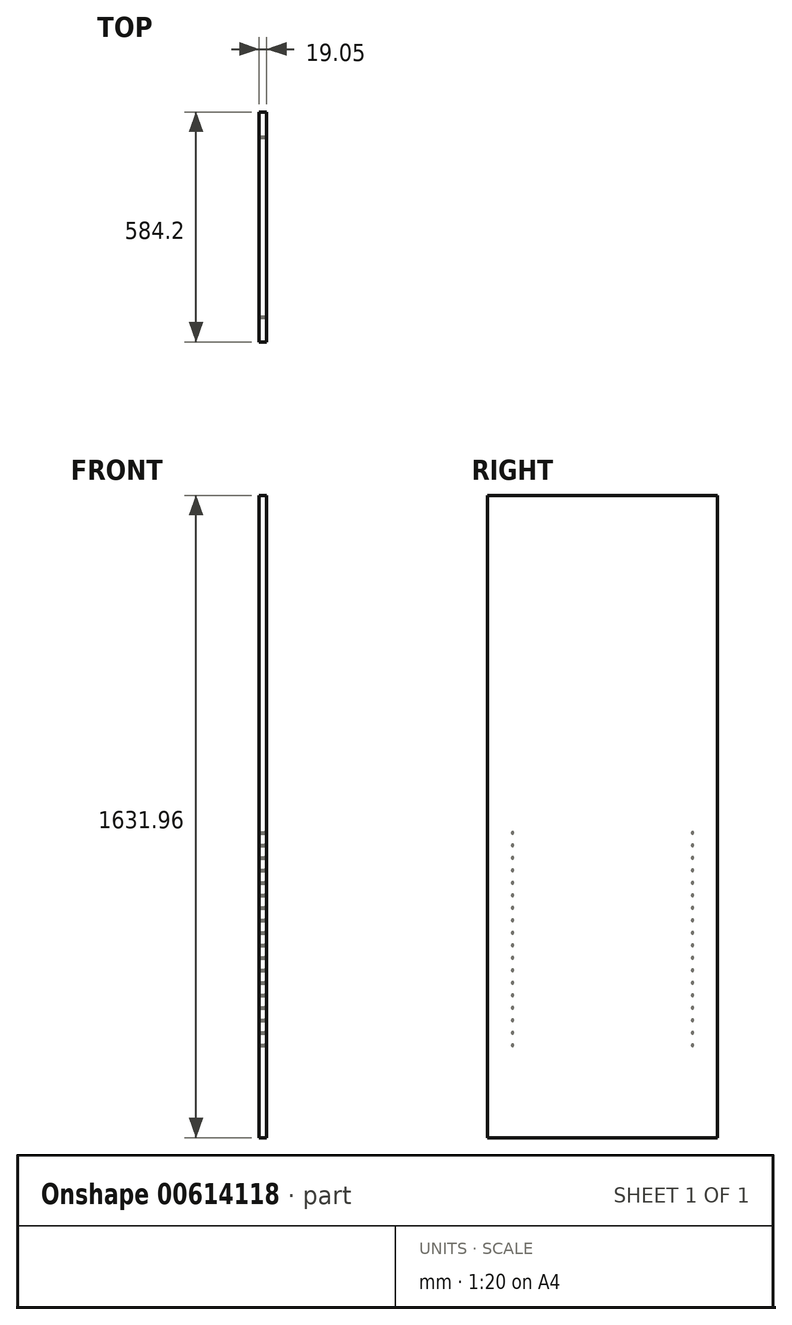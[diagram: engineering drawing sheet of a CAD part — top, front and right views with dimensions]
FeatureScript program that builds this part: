
annotation { "Feature Type Name" : "Feature", "Feature Type Description" : "" }
export const myFeature = defineFeature(function(context is Context, id is Id, definition is map)
    precondition{}
    {
        {
            var Q0;
            Q0=qCreatedBy(makeId("Right.planeOp"),FACE);
            var sketch = newSketch(context, id + "F0", { "sketchPlane" : qUnion([Q0])});
            skLineSegment(sketch, "E0.bottom", {"start": v(292.1, 815.98) * mm, "end": v(-292.1, 815.98) * mm});
            skLineSegment(sketch, "E0.top", {"start": v(292.1, -815.98) * mm, "end": v(-292.1, -815.98) * mm});
            skLineSegment(sketch, "E0.left", {"start": v(292.1, 815.98) * mm, "end": v(292.1, -815.98) * mm});
            skLineSegment(sketch, "E0.right", {"start": v(-292.1, 815.98) * mm, "end": v(-292.1, -815.98) * mm});
            skPoint(sketch, "E0.middle", {"position": v(0, 0) * mm});
            skSolve(sketch);
        }
        {
            var Q0;
            Q0=makeQuery(id+"F0.imprint","IMPRINT",FACE,{"disambiguationData":[TD([[makeQuery(id+"F0.imprint","IMPRINT",EDGE,{"derivedFrom":sQuery(id+"F0.wireOp",EDGE,"E0.bottom")}),1.0]])]});
            extrude(context, id + "F1", {"entities" : qUnion([Q0]), "depth" : 19.05 * mm, "offsetDistance" : 25.4 * mm});
        }
        {
            var Q0;
            Q0=makeQuery(id+"F1.opExtrude","CAP_FACE",FACE,{"disambiguationData":[OSD([sQuery(id+"F0.wireOp",EDGE,"E0.bottom"),sQuery(id+"F0.wireOp",EDGE,"E0.top"),sQuery(id+"F0.wireOp",EDGE,"E0.left"),sQuery(id+"F0.wireOp",EDGE,"E0.right")])],"isStart":true});
            var sketch = newSketch(context, id + "F2", { "sketchPlane" : qUnion([Q0])});
            skLineSegment(sketch, "E1", {"start": v(0, -815.98) * mm, "end": v(0, -549.27) * mm});
            skLineSegment(sketch, "E2.bottom", {"start": v(228.6, -517.52) * mm, "end": v(-228.6, -517.52) * mm});
            skLineSegment(sketch, "E2.top", {"start": v(228.6, -581.02) * mm, "end": v(-228.6, -581.02) * mm});
            skLineSegment(sketch, "E2.left", {"start": v(228.6, -517.52) * mm, "end": v(228.6, -581.02) * mm});
            skLineSegment(sketch, "E2.right", {"start": v(-228.6, -517.52) * mm, "end": v(-228.6, -581.02) * mm});
            skPoint(sketch, "E2.middle", {"position": v(0, -549.27) * mm});
            skLineSegment(sketch, "E3", {"start": v(0, -517.52) * mm, "end": v(0, -454.02) * mm});
            skPoint(sketch, "E3.endSnap0", {"position": v(0, -517.52) * mm});
            skLineSegment(sketch, "E4.bottom", {"start": v(228.6, -422.27) * mm, "end": v(-228.6, -422.27) * mm});
            skLineSegment(sketch, "E4.top", {"start": v(228.6, -485.77) * mm, "end": v(-228.6, -485.77) * mm});
            skLineSegment(sketch, "E4.left", {"start": v(228.6, -422.27) * mm, "end": v(228.6, -485.77) * mm});
            skLineSegment(sketch, "E4.right", {"start": v(-228.6, -422.27) * mm, "end": v(-228.6, -485.77) * mm});
            skPoint(sketch, "E4.middle", {"position": v(0, -454.02) * mm});
            skLineSegment(sketch, "E5", {"start": v(0, -422.27) * mm, "end": v(0, -358.77) * mm});
            skPoint(sketch, "E5.endSnap0", {"position": v(0, -422.27) * mm});
            skLineSegment(sketch, "E6.bottom", {"start": v(228.6, -327.02) * mm, "end": v(-228.6, -327.02) * mm});
            skLineSegment(sketch, "E6.top", {"start": v(228.6, -390.52) * mm, "end": v(-228.6, -390.52) * mm});
            skLineSegment(sketch, "E6.left", {"start": v(228.6, -327.02) * mm, "end": v(228.6, -390.52) * mm});
            skLineSegment(sketch, "E6.right", {"start": v(-228.6, -327.02) * mm, "end": v(-228.6, -390.52) * mm});
            skPoint(sketch, "E6.middle", {"position": v(0, -358.77) * mm});
            skLineSegment(sketch, "E7", {"start": v(0, -327.02) * mm, "end": v(0, -263.52) * mm});
            skPoint(sketch, "E7.endSnap0", {"position": v(0, -327.02) * mm});
            skLineSegment(sketch, "E8.bottom", {"start": v(228.6, -231.77) * mm, "end": v(-228.6, -231.77) * mm});
            skLineSegment(sketch, "E8.top", {"start": v(228.6, -295.27) * mm, "end": v(-228.6, -295.27) * mm});
            skLineSegment(sketch, "E8.left", {"start": v(228.6, -231.77) * mm, "end": v(228.6, -295.27) * mm});
            skLineSegment(sketch, "E8.right", {"start": v(-228.6, -231.77) * mm, "end": v(-228.6, -295.27) * mm});
            skPoint(sketch, "E8.middle", {"position": v(0, -263.52) * mm});
            skLineSegment(sketch, "E9", {"start": v(0, -231.77) * mm, "end": v(0, -168.27) * mm});
            skPoint(sketch, "E9.endSnap0", {"position": v(0, -231.77) * mm});
            skLineSegment(sketch, "E10.bottom", {"start": v(228.6, -200.02) * mm, "end": v(-228.6, -200.02) * mm});
            skLineSegment(sketch, "E10.top", {"start": v(228.6, -136.52) * mm, "end": v(-228.6, -136.52) * mm});
            skLineSegment(sketch, "E10.left", {"start": v(228.6, -200.02) * mm, "end": v(228.6, -136.52) * mm});
            skLineSegment(sketch, "E10.right", {"start": v(-228.6, -200.02) * mm, "end": v(-228.6, -136.52) * mm});
            skPoint(sketch, "E10.middle", {"position": v(0, -168.27) * mm});
            skLineSegment(sketch, "E11", {"start": v(0, -136.52) * mm, "end": v(0, -73.02) * mm});
            skLineSegment(sketch, "E12.bottom", {"start": v(228.6, -41.27) * mm, "end": v(-228.6, -41.27) * mm});
            skLineSegment(sketch, "E12.top", {"start": v(228.6, -104.77) * mm, "end": v(-228.6, -104.77) * mm});
            skLineSegment(sketch, "E12.left", {"start": v(228.6, -41.27) * mm, "end": v(228.6, -104.77) * mm});
            skLineSegment(sketch, "E12.right", {"start": v(-228.6, -41.27) * mm, "end": v(-228.6, -104.77) * mm});
            skPoint(sketch, "E12.middle", {"position": v(0, -73.02) * mm});
            skPoint(sketch, "E13", {"position": v(228.6, -41.27) * mm});
            skPoint(sketch, "E14", {"position": v(228.6, -73.02) * mm});
            skPoint(sketch, "E15", {"position": v(228.6, -104.77) * mm});
            skPoint(sketch, "E16", {"position": v(228.6, -136.52) * mm});
            skPoint(sketch, "E17", {"position": v(228.6, -168.27) * mm});
            skPoint(sketch, "E18", {"position": v(228.6, -231.77) * mm});
            skPoint(sketch, "E19", {"position": v(228.6, -200.02) * mm});
            skPoint(sketch, "E20", {"position": v(228.6, -263.52) * mm});
            skPoint(sketch, "E21", {"position": v(228.6, -295.27) * mm});
            skPoint(sketch, "E22", {"position": v(228.6, -327.02) * mm});
            skPoint(sketch, "E23", {"position": v(228.6, -358.77) * mm});
            skPoint(sketch, "E24", {"position": v(228.6, -390.52) * mm});
            skPoint(sketch, "E25", {"position": v(228.6, -422.27) * mm});
            skPoint(sketch, "E26", {"position": v(228.6, -454.02) * mm});
            skPoint(sketch, "E27", {"position": v(228.6, -485.77) * mm});
            skPoint(sketch, "E28", {"position": v(228.6, -517.52) * mm});
            skPoint(sketch, "E29", {"position": v(228.6, -549.27) * mm});
            skPoint(sketch, "E30", {"position": v(228.6, -581.02) * mm});
            skPoint(sketch, "E31", {"position": v(-228.6, -41.27) * mm});
            skPoint(sketch, "E32", {"position": v(-228.6, -73.02) * mm});
            skPoint(sketch, "E33", {"position": v(-228.6, -104.77) * mm});
            skPoint(sketch, "E34", {"position": v(-228.6, -136.52) * mm});
            skPoint(sketch, "E35", {"position": v(-228.6, -168.27) * mm});
            skPoint(sketch, "E36", {"position": v(-228.6, -200.02) * mm});
            skPoint(sketch, "E37", {"position": v(-228.6, -231.77) * mm});
            skPoint(sketch, "E38", {"position": v(-228.6, -263.52) * mm});
            skPoint(sketch, "E39", {"position": v(-228.6, -295.27) * mm});
            skPoint(sketch, "E40", {"position": v(-228.6, -327.02) * mm});
            skPoint(sketch, "E41", {"position": v(-228.6, -358.77) * mm});
            skPoint(sketch, "E42", {"position": v(-228.6, -390.52) * mm});
            skPoint(sketch, "E43", {"position": v(-228.6, -422.27) * mm});
            skPoint(sketch, "E44", {"position": v(-228.6, -454.02) * mm});
            skPoint(sketch, "E45", {"position": v(-228.6, -485.77) * mm});
            skPoint(sketch, "E46", {"position": v(-228.6, -517.52) * mm});
            skPoint(sketch, "E47", {"position": v(-228.6, -549.27) * mm});
            skPoint(sketch, "E48", {"position": v(-228.6, -581.02) * mm});
            skSolve(sketch);
        }
        {
            var Q0;
            Q0=sQuery(id+"F2.wireOp",VERTEX,"E31");
            var Q1;
            Q1=sQuery(id+"F2.wireOp",VERTEX,"E32");
            var Q2;
            Q2=sQuery(id+"F2.wireOp",VERTEX,"E33");
            var Q3;
            Q3=sQuery(id+"F2.wireOp",VERTEX,"E34");
            var Q4;
            Q4=sQuery(id+"F2.wireOp",VERTEX,"E35");
            var Q5;
            Q5=sQuery(id+"F2.wireOp",VERTEX,"E36");
            var Q6;
            Q6=sQuery(id+"F2.wireOp",VERTEX,"E37");
            var Q7;
            Q7=sQuery(id+"F2.wireOp",VERTEX,"E38");
            var Q8;
            Q8=sQuery(id+"F2.wireOp",VERTEX,"E39");
            var Q9;
            Q9=sQuery(id+"F2.wireOp",VERTEX,"E40");
            var Q10;
            Q10=sQuery(id+"F2.wireOp",VERTEX,"E41");
            var Q11;
            Q11=sQuery(id+"F2.wireOp",VERTEX,"E42");
            var Q12;
            Q12=sQuery(id+"F2.wireOp",VERTEX,"E43");
            var Q13;
            Q13=sQuery(id+"F2.wireOp",VERTEX,"E45");
            var Q14;
            Q14=sQuery(id+"F2.wireOp",VERTEX,"E46");
            var Q15;
            Q15=sQuery(id+"F2.wireOp",VERTEX,"E47");
            var Q16;
            Q16=sQuery(id+"F2.wireOp",VERTEX,"E48");
            var Q17;
            Q17=sQuery(id+"F2.wireOp",VERTEX,"E44");
            var Q18;
            Q18=sQuery(id+"F2.wireOp",VERTEX,"E13");
            var Q19;
            Q19=sQuery(id+"F2.wireOp",VERTEX,"E14");
            var Q20;
            Q20=sQuery(id+"F2.wireOp",VERTEX,"E15");
            var Q21;
            Q21=sQuery(id+"F2.wireOp",VERTEX,"E16");
            var Q22;
            Q22=sQuery(id+"F2.wireOp",VERTEX,"E17");
            var Q23;
            Q23=sQuery(id+"F2.wireOp",VERTEX,"E19");
            var Q24;
            Q24=sQuery(id+"F2.wireOp",VERTEX,"E18");
            var Q25;
            Q25=sQuery(id+"F2.wireOp",VERTEX,"E20");
            var Q26;
            Q26=sQuery(id+"F2.wireOp",VERTEX,"E21");
            var Q27;
            Q27=sQuery(id+"F2.wireOp",VERTEX,"E22");
            var Q28;
            Q28=sQuery(id+"F2.wireOp",VERTEX,"E23");
            var Q29;
            Q29=sQuery(id+"F2.wireOp",VERTEX,"E24");
            var Q30;
            Q30=sQuery(id+"F2.wireOp",VERTEX,"E25");
            var Q31;
            Q31=sQuery(id+"F2.wireOp",VERTEX,"E26");
            var Q32;
            Q32=sQuery(id+"F2.wireOp",VERTEX,"E27");
            var Q33;
            Q33=sQuery(id+"F2.wireOp",VERTEX,"E28");
            var Q34;
            Q34=sQuery(id+"F2.wireOp",VERTEX,"E29");
            var Q35;
            Q35=sQuery(id+"F2.wireOp",VERTEX,"E30");
            var Q36;
            Q36=sQuery(id+"F2.wireOp",VERTEX,"E21");
            var Q37;
            Q37=sQuery(id+"F2.wireOp",VERTEX,"E22");
            var Q38;
            Q38=sQuery(id+"F2.wireOp",VERTEX,"E23");
            var Q39;
            Q39=sQuery(id+"F2.wireOp",VERTEX,"E24");
            var Q40;
            Q40=sQuery(id+"F2.wireOp",VERTEX,"E25");
            var Q41;
            Q41=sQuery(id+"F2.wireOp",VERTEX,"E26");
            var Q42;
            Q42=sQuery(id+"F2.wireOp",VERTEX,"E27");
            var Q43;
            Q43=sQuery(id+"F2.wireOp",VERTEX,"E28");
            var Q44;
            Q44=sQuery(id+"F2.wireOp",VERTEX,"E29");
            var Q45;
            Q45=sQuery(id+"F2.wireOp",VERTEX,"E30");
            var Q46;
            Q46=makeQuery(id+"F1.opExtrude","SWEPT_BODY",BODY,{"disambiguationData":[OSD([sQuery(id+"F0.wireOp",EDGE,"E0.bottom"),sQuery(id+"F0.wireOp",EDGE,"E0.top"),sQuery(id+"F0.wireOp",EDGE,"E0.left"),sQuery(id+"F0.wireOp",EDGE,"E0.right")])]});
            hole(context, id + "F3", {"style" : HoleStyle.SIMPLE, "endStyle" : HoleEndStyle.BLIND, "holeDiameter" : 5 * mm, "majorDiameter" : 6.35 * mm, "holeDepth" : 14.22 * mm, "isTappedThrough" : true, "tappedDepth" : 12.7 * mm, "tapClearance" : 3, "startFromSketch" : true, "locations" : qUnion([Q0, Q1, Q2, Q3, Q4, Q5, Q6, Q7, Q8, Q9, Q10, Q11, Q12, Q13, Q14, Q15, Q16, Q17, Q18, Q19, Q20, Q21, Q22, Q23, Q24, Q25, Q26, Q27, Q28, Q29, Q30, Q31, Q32, Q33, Q34, Q35, Q36, Q37, Q38, Q39, Q40, Q41, Q42, Q43, Q44, Q45]), "scope" : qUnion([Q46])});
        }
    });
